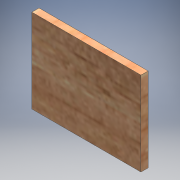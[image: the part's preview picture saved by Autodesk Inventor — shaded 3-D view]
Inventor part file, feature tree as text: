
AUTODESK INVENTOR PART (.ipt)
format: ipt  version: 2016 (Build 200138000, 138)  size: 121,856 bytes
history: native  units: mm
features: sketch x2, extrude x1, hole x1
ambient origin geometry x8: Origin, YZ Plane, XZ Plane, XY Plane, X Axis, Y Axis, Z Axis, Center Point
bodies: Solid1 (feature_tree)
feature tree (4):
  extrude  "Extrusion1"  Depth=35.0mm
  hole  "Hole1"  [1 undecoded]
  sketch  "Sketch1"  dims[d0=45.5mm d1=35.0mm]
  sketch  "Sketch2"  dims[d2=3.0mm d3=0.0mm d4=2.0mm d5=6.0mm d6=1.5mm d7=2.0mm d8=6.0mm d9=4.0mm d10=2.0mm d11=90.0deg d12=8.0mm d13=20.594885mm]
note: 1 required parameter value undecoded (feature->parameter linkage not recoverable at this tier; creation-order binding heuristic only, values carry confidence <= 0.55)
